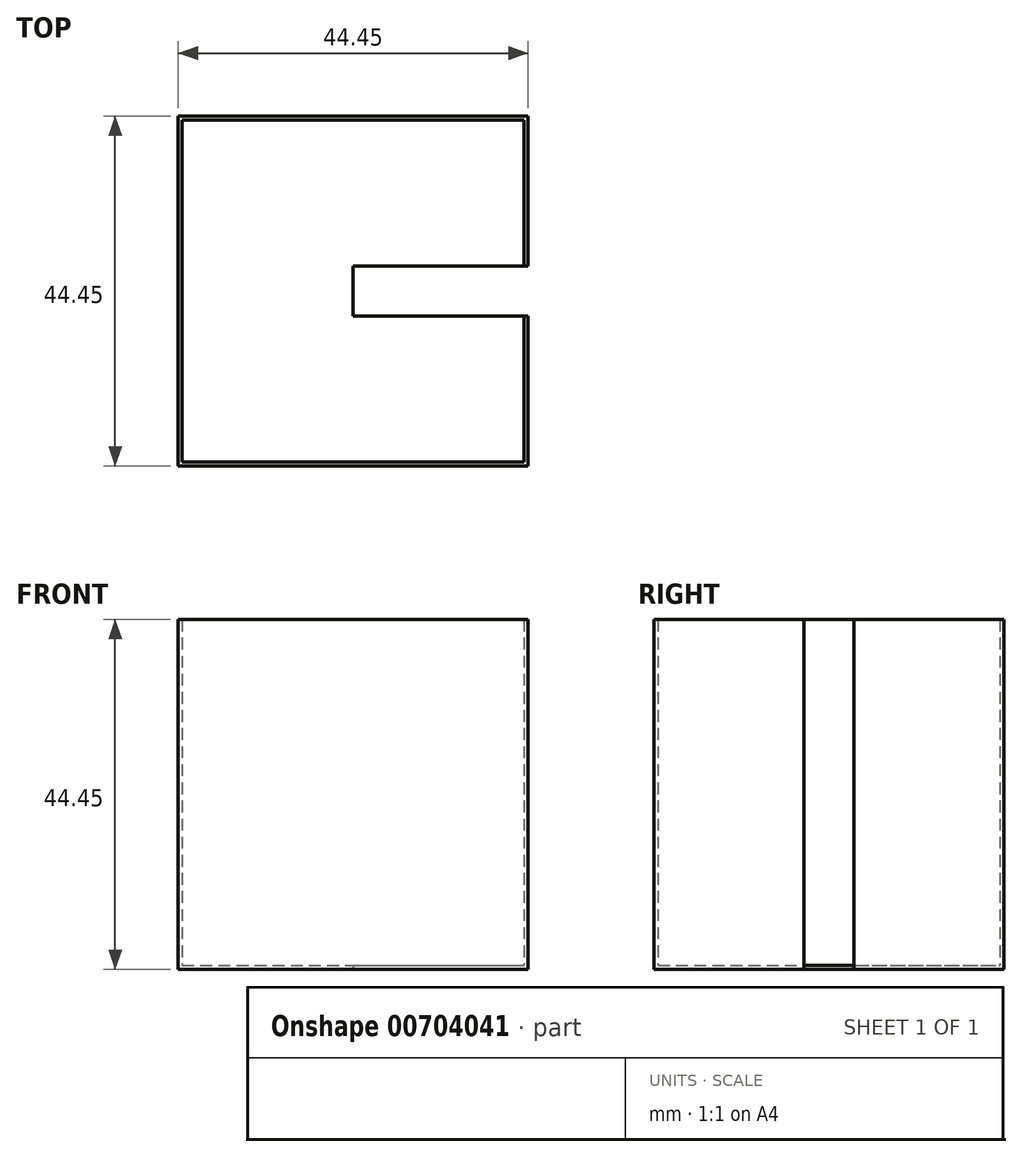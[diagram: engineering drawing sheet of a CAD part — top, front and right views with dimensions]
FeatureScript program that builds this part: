
annotation { "Feature Type Name" : "Feature", "Feature Type Description" : "" }
export const myFeature = defineFeature(function(context is Context, id is Id, definition is map)
    precondition{}
    {
        {
            var Q0;
            Q0=qCreatedBy(makeId("Top.planeOp"),FACE);
            var sketch = newSketch(context, id + "F0", { "sketchPlane" : qUnion([Q0])});
            skLineSegment(sketch, "E0.bottom", {"start": v(0, 0) * mm, "end": v(44.45, 0) * mm});
            skLineSegment(sketch, "E0.top", {"start": v(0, 44.45) * mm, "end": v(44.45, 44.45) * mm});
            skLineSegment(sketch, "E0.left", {"start": v(0, 0) * mm, "end": v(0, 44.45) * mm});
            skLineSegment(sketch, "E0.right", {"start": v(44.45, 0) * mm, "end": v(44.45, 19.05) * mm});
            skLineSegment(sketch, "E1", {"start": v(44.45, 19.05) * mm, "end": v(22.23, 19.05) * mm});
            skLineSegment(sketch, "E2", {"start": v(22.23, 19.05) * mm, "end": v(22.23, 25.4) * mm});
            skLineSegment(sketch, "E3", {"start": v(22.23, 25.4) * mm, "end": v(44.45, 25.4) * mm});
            skLineSegment(sketch, "E4.trimOffspring", {"start": v(44.45, 25.4) * mm, "end": v(44.45, 44.45) * mm});
            skSolve(sketch);
        }
        {
            var Q0;
            Q0=makeQuery(id+"F0.imprint","IMPRINT",FACE,{"disambiguationData":[TD([[makeQuery(id+"F0.imprint","IMPRINT",EDGE,{"derivedFrom":sQuery(id+"F0.wireOp",EDGE,"E0.bottom")}),1.0]])]});
            extrude(context, id + "F1", {"entities" : qUnion([Q0]), "depth" : 44.45 * mm, "offsetDistance" : 25.4 * mm});
        }
        {
            var Q0;
            Q0=makeQuery(id+"F1.opExtrude","CAP_FACE",FACE,{"disambiguationData":[OSD([sQuery(id+"F0.wireOp",EDGE,"E0.bottom"),sQuery(id+"F0.wireOp",EDGE,"E0.top"),sQuery(id+"F0.wireOp",EDGE,"E0.left"),sQuery(id+"F0.wireOp",EDGE,"E0.right"),sQuery(id+"F0.wireOp",EDGE,"E1"),sQuery(id+"F0.wireOp",EDGE,"E2"),sQuery(id+"F0.wireOp",EDGE,"E3"),sQuery(id+"F0.wireOp",EDGE,"E4.trimOffspring")])],"isStart":false});
            var Q1;
            Q1=makeQuery(id+"F1.opExtrude","SWEPT_FACE",FACE,{"disambiguationData":[OSD([sQuery(id+"F0.wireOp",EDGE,"E2")])]});
            var Q2;
            Q2=makeQuery(id+"F1.opExtrude","SWEPT_FACE",FACE,{"disambiguationData":[OSD([sQuery(id+"F0.wireOp",EDGE,"E3")])]});
            var Q3;
            Q3=makeQuery(id+"F1.opExtrude","SWEPT_FACE",FACE,{"disambiguationData":[OSD([sQuery(id+"F0.wireOp",EDGE,"E1")])]});
            shell(context, id + "F2", {"entities" : qUnion([Q0, Q1, Q2, Q3]), "thickness" : 0.5 * mm});
        }
        {
            var Q0;
            Q0=makeQuery(id+"F1.opExtrude","SWEPT_FACE",FACE,{"disambiguationData":[OSD([sQuery(id+"F0.wireOp",EDGE,"E0.bottom")])]});
            var sketch = newSketch(context, id + "F3", { "sketchPlane" : qUnion([Q0])});
            skCircle(sketch, "E5", {"center": v(-3.17, 42.04) * mm, "radius": 3.18 * mm});
            skSolve(sketch);
        }
        {
            var Q0;
            Q0=sQuery(id+"F3.wireOp",EDGE,"E5");
            extrude(context, id + "F4", {"bodyType" : ToolBodyType.SURFACE, "operationType" : NewBodyOperationType.INTERSECT, "surfaceEntities" : qUnion([Q0]), "depth" : 12.7 * mm, "offsetDistance" : 25.4 * mm, "hasSecondDirection" : true, "secondDirectionOppositeDirection" : true, "secondDirectionDepth" : 57.15 * mm});
        }
    });
